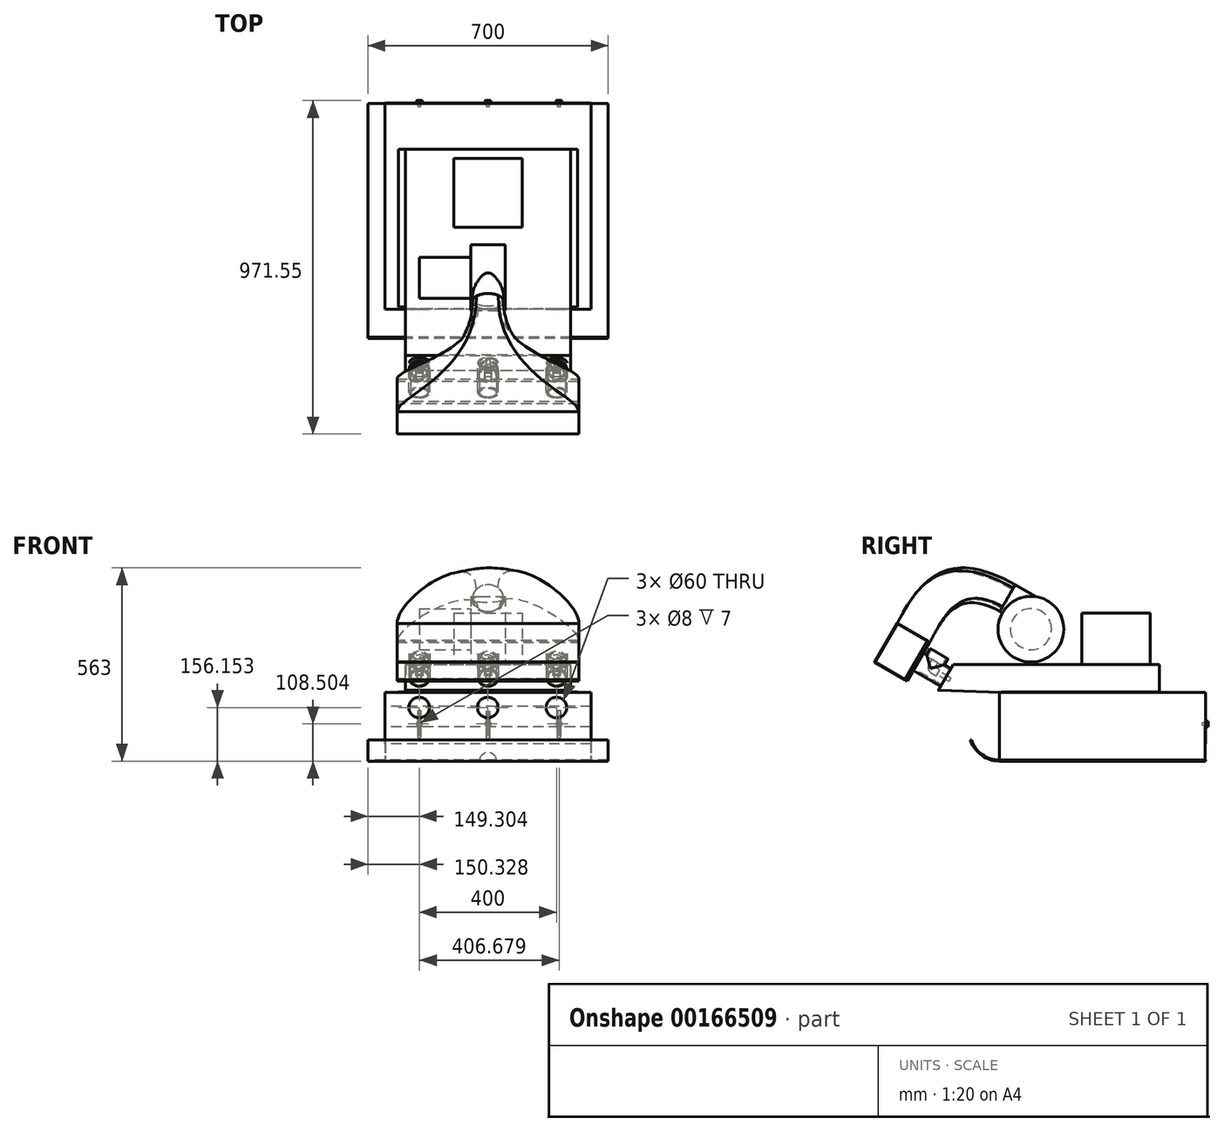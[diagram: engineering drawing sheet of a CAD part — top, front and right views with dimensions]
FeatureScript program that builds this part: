
annotation { "Feature Type Name" : "Feature", "Feature Type Description" : "" }
export const myFeature = defineFeature(function(context is Context, id is Id, definition is map)
    precondition{}
    {
        {
            assignVariable(context, id + "F0", {"name" : "Width", "anyValue" : 600});
        }
        {
            assignVariable(context, id + "F1", {"name" : "Height", "anyValue" : 200});
        }
        {
            var Q0;
            Q0=qCreatedBy(makeId("Top.planeOp"),FACE);
            var sketch = newSketch(context, id + "F2", { "sketchPlane" : qUnion([Q0])});
            skLineSegment(sketch, "E0.bottom", {"start": v(300, -300) * mm, "end": v(-300, -300) * mm});
            skLineSegment(sketch, "E0.top", {"start": v(300, 300) * mm, "end": v(-300, 300) * mm});
            skLineSegment(sketch, "E0.left", {"start": v(300, -300) * mm, "end": v(300, 300) * mm});
            skLineSegment(sketch, "E0.right", {"start": v(-300, -300) * mm, "end": v(-300, 300) * mm});
            skPoint(sketch, "E0.middle", {"position": v(0, 0) * mm});
            skSolve(sketch);
        }
        {
            var Q0;
            Q0 = qSketchRegion(id + "F2", true);
            extrude(context, id + "F3", {"entities" : qUnion([Q0]), "depth" : (getVariable(context, 'Height')) * mm});
        }
        {
            var Q0;
            Q0=makeQuery(id+"F3.opExtrude","CAP_FACE",FACE,{"disambiguationData":[OSD([sQuery(id+"F2.wireOp",EDGE,"E0.bottom"),sQuery(id+"F2.wireOp",EDGE,"E0.top"),sQuery(id+"F2.wireOp",EDGE,"E0.left"),sQuery(id+"F2.wireOp",EDGE,"E0.right")])],"isStart":true});
            shell(context, id + "F4", {"entities" : qUnion([Q0]), "thickness" : 1 * mm});
        }
        {
            var Q0;
            Q0=qCreatedBy(makeId("Front.planeOp"),FACE);
            var sketch = newSketch(context, id + "F5", { "sketchPlane" : qUnion([Q0])});
            skCircle(sketch, "E1", {"center": v(0, 0) * mm, "radius": 25 * mm});
            skCircle(sketch, "E2", {"center": v(0, 0) * mm, "radius": 23.4 * mm});
            skSolve(sketch);
        }
        {
            var Q0;
            Q0 = qSketchRegion(id + "F5", true);
            extrude(context, id + "F6", {"entities" : qUnion([Q0]), "depth" : 200 * mm});
        }
        {
            var Q0;
            Q0=makeQuery(id+"F6.opExtrude","CAP_FACE",FACE,{"disambiguationData":[OSD([sQuery(id+"F5.wireOp",EDGE,"E1"),sQuery(id+"F5.wireOp",EDGE,"E2")])],"isStart":false});
            var sketch = newSketch(context, id + "F7", { "sketchPlane" : qUnion([Q0])});
            skCircle(sketch, "E3", {"center": v(0, 0) * mm, "radius": 30 * mm});
            skSolve(sketch);
        }
        {
            var Q0;
            Q0 = qSketchRegion(id + "F7", true);
            extrude(context, id + "F8", {"entities" : qUnion([Q0]), "depth" : 100 * mm});
        }
        {
            var Q0;
            Q0=qCreatedBy(makeId("Top.planeOp"),FACE);
            var sketch = newSketch(context, id + "F9", { "sketchPlane" : qUnion([Q0])});
            skCircle(sketch, "E4", {"center": v(0, -251.88) * mm, "radius": 30 * mm});
            skSolve(sketch);
        }
        {
            var Q0;
            Q0 = qSketchRegion(id + "F9", true);
            extrude(context, id + "F10", {"entities" : qUnion([Q0]), "operationType" : NewBodyOperationType.ADD, "depth" : 50 * mm});
        }
        {
            var Q0;
            Q0=makeQuery(id+"F10.opExtrude","CAP_FACE",FACE,{"disambiguationData":[OSD([sQuery(id+"F9.wireOp",EDGE,"E4")])],"isStart":false});
            var sketch = newSketch(context, id + "F11", { "sketchPlane" : qUnion([Q0])});
            skCircle(sketch, "E5", {"center": v(0, -251.88) * mm, "radius": 25 * mm});
            skSolve(sketch);
        }
        {
            var Q0;
            Q0=makeQuery(id+"F8.opExtrude","CAP_FACE",FACE,{"disambiguationData":[OSD([sQuery(id+"F7.wireOp",EDGE,"E3")])],"isStart":false});
            var sketch = newSketch(context, id + "F12", { "sketchPlane" : qUnion([Q0])});
            skCircle(sketch, "E6", {"center": v(0, 0) * mm, "radius": 25 * mm});
            skSolve(sketch);
        }
        {
            var Q0;
            Q0 = qSketchRegion(id + "F12", true);
            extrude(context, id + "F13", {"entities" : qUnion([Q0]), "operationType" : NewBodyOperationType.REMOVE, "endBound" : BoundingType.THROUGH_ALL, "oppositeDirection" : true, "depth" : 25 * mm});
        }
        {
            var Q0;
            Q0 = qSketchRegion(id + "F11", true);
            extrude(context, id + "F14", {"entities" : qUnion([Q0]), "operationType" : NewBodyOperationType.REMOVE, "endBound" : BoundingType.UP_TO_NEXT, "oppositeDirection" : true, "depth" : 25 * mm});
        }
        {
            var Q0;
            Q0=makeQuery(id+"F10.opExtrude","CAP_FACE",FACE,{"disambiguationData":[OSD([sQuery(id+"F9.wireOp",EDGE,"E4")])],"isStart":false});
            var sketch = newSketch(context, id + "F15", { "sketchPlane" : qUnion([Q0])});
            skCircle(sketch, "E7", {"center": v(0, -251.88) * mm, "radius": 25 * mm});
            skSolve(sketch);
        }
        {
            var Q0;
            Q0 = qSketchRegion(id + "F15", true);
            extrude(context, id + "F16", {"entities" : qUnion([Q0]), "oppositeDirection" : true, "depth" : 25 * mm});
        }
        {
            var Q0;
            Q0=qCreatedBy(makeId("Right.planeOp"),FACE);
            var sketch = newSketch(context, id + "F17", { "sketchPlane" : qUnion([Q0])});
            skLineSegment(sketch, "E8", {"start": v(-261.88, 25) * mm, "end": v(-261.88, 7.92) * mm});
            skLineSegment(sketch, "E9", {"start": v(-243.95, -10) * mm, "end": v(-226.88, -10) * mm});
            skLineSegment(sketch, "E10", {"start": v(-226.88, -10) * mm, "end": v(-226.88, 10) * mm});
            skLineSegment(sketch, "E11", {"start": v(-241.88, 12.68) * mm, "end": v(-241.88, 25) * mm});
            skLineSegment(sketch, "E12", {"start": v(-241.88, 25) * mm, "end": v(-261.88, 25) * mm});
            skLineSegment(sketch, "E13.0", {"start": v(-276.88, 25) * mm, "end": v(-226.88, 25) * mm});
            skLineSegment(sketch, "E14", {"start": v(-251.88, 25) * mm, "end": v(-251.88, -30.53) * mm, "construction": true});
            skLineSegment(sketch, "E15.0", {"start": v(-200, -25) * mm, "end": v(-200, 25) * mm});
            skLineSegment(sketch, "E16", {"start": v(-200, 0) * mm, "end": v(-302.48, 0) * mm, "construction": true});
            skPoint(sketch, "E16.endSnap0", {"position": v(-200, 0) * mm});
            skArc(sketch, "E17", {"start": v(-243.95, -10) * mm, "mid": v(-256.63, -4.75) * mm, "end": v(-261.88, 7.92) * mm});
            skLineSegment(sketch, "E18", {"start": v(-226.88, 10) * mm, "end": v(-239.2, 10) * mm});
            skArc(sketch, "E19", {"start": v(-239.2, 10) * mm, "mid": v(-241.1, 10.79) * mm, "end": v(-241.88, 12.68) * mm});
            skSolve(sketch);
        }
        {
            var Q0;
            Q0 = qSketchRegion(id + "F17", true);
            extrude(context, id + "F18", {"entities" : qUnion([Q0]), "endBound" : BoundingType.SYMMETRIC, "depth" : 20 * mm});
        }
        {
            var Q0;
            Q0=makeQuery(id+"F18.opExtrude","SWEPT_FACE",FACE,{"disambiguationData":[OSD([sQuery(id+"F17.wireOp",EDGE,"E10")])]});
            var sketch = newSketch(context, id + "F19", { "sketchPlane" : qUnion([Q0])});
            skCircle(sketch, "E20", {"center": v(0, 0) * mm, "radius": 6 * mm});
            skSolve(sketch);
        }
        {
            var Q0;
            Q0 = qSketchRegion(id + "F19", true);
            extrude(context, id + "F20", {"entities" : qUnion([Q0]), "depth" : 40 * mm});
        }
        {
            var Q0;
            Q0=makeQuery(id+"F6.opExtrude","SWEPT_BODY",BODY,{"disambiguationData":[OSD([sQuery(id+"F5.wireOp",EDGE,"E1"),sQuery(id+"F5.wireOp",EDGE,"E2")])]});
            var Q1;
            Q1=makeQuery(id+"F8.opExtrude","SWEPT_BODY",BODY,{"disambiguationData":[OSD([sQuery(id+"F7.wireOp",EDGE,"E3")])]});
            var Q2;
            Q2=makeQuery(id+"F16.opExtrude","SWEPT_BODY",BODY,{"disambiguationData":[OSD([sQuery(id+"F15.wireOp",EDGE,"E7")])]});
            var Q3;
            Q3=makeQuery(id+"F18.opExtrude","SWEPT_BODY",BODY,{"disambiguationData":[OSD([sQuery(id+"F17.wireOp",EDGE,"E8"),sQuery(id+"F17.wireOp",EDGE,"E9"),sQuery(id+"F17.wireOp",EDGE,"E10"),sQuery(id+"F17.wireOp",EDGE,"E11"),sQuery(id+"F17.wireOp",EDGE,"E13.0"),sQuery(id+"F17.wireOp",EDGE,"E17"),sQuery(id+"F17.wireOp",EDGE,"E18"),sQuery(id+"F17.wireOp",EDGE,"E19")])]});
            var Q4;
            Q4=makeQuery(id+"F20.opExtrude","SWEPT_BODY",BODY,{"disambiguationData":[OSD([sQuery(id+"F19.wireOp",EDGE,"E20")])]});
            transform(context, id + "F21", {"entities" : qUnion([Q0, Q1, Q2, Q3, Q4]), "transformType" : TransformType.TRANSLATION_3D, "dx" : 0 * mm, "dy" : -282 * mm, "dz" : 163 * mm, "makeCopy" : false});
        }
        {
            var Q0;
            Q0=makeQuery(id+"F6.opExtrude","SWEPT_BODY",BODY,{"disambiguationData":[OSD([sQuery(id+"F5.wireOp",EDGE,"E1"),sQuery(id+"F5.wireOp",EDGE,"E2")])]});
            var Q1;
            Q1=makeQuery(id+"F8.opExtrude","SWEPT_BODY",BODY,{"disambiguationData":[OSD([sQuery(id+"F7.wireOp",EDGE,"E3")])]});
            var Q2;
            Q2=makeQuery(id+"F16.opExtrude","SWEPT_BODY",BODY,{"disambiguationData":[OSD([sQuery(id+"F15.wireOp",EDGE,"E7")])]});
            var Q3;
            Q3=makeQuery(id+"F18.opExtrude","SWEPT_BODY",BODY,{"disambiguationData":[OSD([sQuery(id+"F17.wireOp",EDGE,"E8"),sQuery(id+"F17.wireOp",EDGE,"E9"),sQuery(id+"F17.wireOp",EDGE,"E10"),sQuery(id+"F17.wireOp",EDGE,"E11"),sQuery(id+"F17.wireOp",EDGE,"E13.0"),sQuery(id+"F17.wireOp",EDGE,"E17"),sQuery(id+"F17.wireOp",EDGE,"E18"),sQuery(id+"F17.wireOp",EDGE,"E19")])]});
            var Q4;
            Q4=makeQuery(id+"F20.opExtrude","SWEPT_BODY",BODY,{"disambiguationData":[OSD([sQuery(id+"F19.wireOp",EDGE,"E20")])]});
            transform(context, id + "F22", {"entities" : qUnion([Q0, Q1, Q2, Q3, Q4]), "transformType" : TransformType.TRANSLATION_3D, "dx" : 200 * mm, "dy" : 0 * mm, "dz" : 0 * mm, "makeCopy" : true});
        }
        {
            var Q0;
            Q0=makeQuery(id+"F6.opExtrude","SWEPT_BODY",BODY,{"disambiguationData":[OSD([sQuery(id+"F5.wireOp",EDGE,"E1"),sQuery(id+"F5.wireOp",EDGE,"E2")])]});
            var Q1;
            Q1=makeQuery(id+"F8.opExtrude","SWEPT_BODY",BODY,{"disambiguationData":[OSD([sQuery(id+"F7.wireOp",EDGE,"E3")])]});
            var Q2;
            Q2=makeQuery(id+"F16.opExtrude","SWEPT_BODY",BODY,{"disambiguationData":[OSD([sQuery(id+"F15.wireOp",EDGE,"E7")])]});
            var Q3;
            Q3=makeQuery(id+"F18.opExtrude","SWEPT_BODY",BODY,{"disambiguationData":[OSD([sQuery(id+"F17.wireOp",EDGE,"E8"),sQuery(id+"F17.wireOp",EDGE,"E9"),sQuery(id+"F17.wireOp",EDGE,"E10"),sQuery(id+"F17.wireOp",EDGE,"E11"),sQuery(id+"F17.wireOp",EDGE,"E13.0"),sQuery(id+"F17.wireOp",EDGE,"E17"),sQuery(id+"F17.wireOp",EDGE,"E18"),sQuery(id+"F17.wireOp",EDGE,"E19")])]});
            var Q4;
            Q4=makeQuery(id+"F20.opExtrude","SWEPT_BODY",BODY,{"disambiguationData":[OSD([sQuery(id+"F19.wireOp",EDGE,"E20")])]});
            transform(context, id + "F23", {"entities" : qUnion([Q0, Q1, Q2, Q3, Q4]), "transformType" : TransformType.TRANSLATION_3D, "dx" : -200 * mm, "dy" : 0 * mm, "dz" : 0 * mm, "makeCopy" : true});
        }
        {
            var Q0;
            Q0=makeQuery(id+"F6.opExtrude","SWEPT_BODY",BODY,{"disambiguationData":[OSD([sQuery(id+"F5.wireOp",EDGE,"E1"),sQuery(id+"F5.wireOp",EDGE,"E2")])]});
            var Q1;
            Q1=makeQuery(id+"F8.opExtrude","SWEPT_BODY",BODY,{"disambiguationData":[OSD([sQuery(id+"F7.wireOp",EDGE,"E3")])]});
            var Q2;
            Q2=makeQuery(id+"F22.opPattern","COPY",BODY,{"derivedFrom":makeQuery(id+"F8.opExtrude","SWEPT_BODY",BODY,{"disambiguationData":[OSD([sQuery(id+"F7.wireOp",EDGE,"E3")])]}),"instanceName":"1"});
            var Q3;
            Q3=makeQuery(id+"F22.opPattern","COPY",BODY,{"derivedFrom":makeQuery(id+"F6.opExtrude","SWEPT_BODY",BODY,{"disambiguationData":[OSD([sQuery(id+"F5.wireOp",EDGE,"E1"),sQuery(id+"F5.wireOp",EDGE,"E2")])]}),"instanceName":"1"});
            var Q4;
            Q4=makeQuery(id+"F23.opPattern","COPY",BODY,{"derivedFrom":makeQuery(id+"F8.opExtrude","SWEPT_BODY",BODY,{"disambiguationData":[OSD([sQuery(id+"F7.wireOp",EDGE,"E3")])]}),"instanceName":"1"});
            var Q5;
            Q5=makeQuery(id+"F23.opPattern","COPY",BODY,{"derivedFrom":makeQuery(id+"F6.opExtrude","SWEPT_BODY",BODY,{"disambiguationData":[OSD([sQuery(id+"F5.wireOp",EDGE,"E1"),sQuery(id+"F5.wireOp",EDGE,"E2")])]}),"instanceName":"1"});
            var Q6;
            Q6=makeQuery(id+"F16.opExtrude","SWEPT_BODY",BODY,{"disambiguationData":[OSD([sQuery(id+"F15.wireOp",EDGE,"E7")])]});
            var Q7;
            Q7=makeQuery(id+"F18.opExtrude","SWEPT_BODY",BODY,{"disambiguationData":[OSD([sQuery(id+"F17.wireOp",EDGE,"E8"),sQuery(id+"F17.wireOp",EDGE,"E9"),sQuery(id+"F17.wireOp",EDGE,"E10"),sQuery(id+"F17.wireOp",EDGE,"E11"),sQuery(id+"F17.wireOp",EDGE,"E13.0"),sQuery(id+"F17.wireOp",EDGE,"E17"),sQuery(id+"F17.wireOp",EDGE,"E18"),sQuery(id+"F17.wireOp",EDGE,"E19")])]});
            var Q8;
            Q8=makeQuery(id+"F20.opExtrude","SWEPT_BODY",BODY,{"disambiguationData":[OSD([sQuery(id+"F19.wireOp",EDGE,"E20")])]});
            var Q9;
            Q9=makeQuery(id+"F22.opPattern","COPY",BODY,{"derivedFrom":makeQuery(id+"F20.opExtrude","SWEPT_BODY",BODY,{"disambiguationData":[OSD([sQuery(id+"F19.wireOp",EDGE,"E20")])]}),"instanceName":"1"});
            var Q10;
            Q10=makeQuery(id+"F22.opPattern","COPY",BODY,{"derivedFrom":makeQuery(id+"F18.opExtrude","SWEPT_BODY",BODY,{"disambiguationData":[OSD([sQuery(id+"F17.wireOp",EDGE,"E8"),sQuery(id+"F17.wireOp",EDGE,"E9"),sQuery(id+"F17.wireOp",EDGE,"E10"),sQuery(id+"F17.wireOp",EDGE,"E11"),sQuery(id+"F17.wireOp",EDGE,"E13.0"),sQuery(id+"F17.wireOp",EDGE,"E17"),sQuery(id+"F17.wireOp",EDGE,"E18"),sQuery(id+"F17.wireOp",EDGE,"E19")])]}),"instanceName":"1"});
            var Q11;
            Q11=makeQuery(id+"F22.opPattern","COPY",BODY,{"derivedFrom":makeQuery(id+"F16.opExtrude","SWEPT_BODY",BODY,{"disambiguationData":[OSD([sQuery(id+"F15.wireOp",EDGE,"E7")])]}),"instanceName":"1"});
            var Q12;
            Q12=makeQuery(id+"F23.opPattern","COPY",BODY,{"derivedFrom":makeQuery(id+"F20.opExtrude","SWEPT_BODY",BODY,{"disambiguationData":[OSD([sQuery(id+"F19.wireOp",EDGE,"E20")])]}),"instanceName":"1"});
            var Q13;
            Q13=makeQuery(id+"F23.opPattern","COPY",BODY,{"derivedFrom":makeQuery(id+"F18.opExtrude","SWEPT_BODY",BODY,{"disambiguationData":[OSD([sQuery(id+"F17.wireOp",EDGE,"E8"),sQuery(id+"F17.wireOp",EDGE,"E9"),sQuery(id+"F17.wireOp",EDGE,"E10"),sQuery(id+"F17.wireOp",EDGE,"E11"),sQuery(id+"F17.wireOp",EDGE,"E13.0"),sQuery(id+"F17.wireOp",EDGE,"E17"),sQuery(id+"F17.wireOp",EDGE,"E18"),sQuery(id+"F17.wireOp",EDGE,"E19")])]}),"instanceName":"1"});
            var Q14;
            Q14=makeQuery(id+"F23.opPattern","COPY",BODY,{"derivedFrom":makeQuery(id+"F16.opExtrude","SWEPT_BODY",BODY,{"disambiguationData":[OSD([sQuery(id+"F15.wireOp",EDGE,"E7")])]}),"instanceName":"1"});
            var Q15;
            Q15=makeQuery(id+"F3.opExtrude","CAP_EDGE",EDGE,{"disambiguationData":[OSD([sQuery(id+"F2.wireOp",EDGE,"E0.bottom")])],"isStart":false});
            transform(context, id + "F24", {"entities" : qUnion([Q0, Q1, Q2, Q3, Q4, Q5, Q6, Q7, Q8, Q9, Q10, Q11, Q12, Q13, Q14]), "transformType" : TransformType.ROTATION, "transformAxis" : qUnion([Q15]), "angle" : 30 * degree, "makeCopy" : false});
        }
        {
            var Q0;
            Q0=makeQuery(id+"F3.opExtrude","SWEPT_FACE",FACE,{"disambiguationData":[OSD([sQuery(id+"F2.wireOp",EDGE,"E0.bottom")])]});
            var sketch = newSketch(context, id + "F25", { "sketchPlane" : qUnion([Q0])});
            skCircle(sketch, "E21", {"center": v(-200.7, 156.15) * mm, "radius": 30 * mm});
            skCircle(sketch, "E22.1.0.0", {"center": v(-0.7, 156.15) * mm, "radius": 30 * mm});
            skCircle(sketch, "E22.2.0.0", {"center": v(199.3, 156.15) * mm, "radius": 30 * mm});
            skLineSegment(sketch, "E22.direction1", {"start": v(-200.7, 156.15) * mm, "end": v(-0.7, 156.15) * mm, "construction": true});
            skSolve(sketch);
        }
        {
            var Q0;
            Q0 = qSketchRegion(id + "F25", true);
            extrude(context, id + "F26", {"entities" : qUnion([Q0]), "operationType" : NewBodyOperationType.REMOVE, "oppositeDirection" : true, "depth" : 25 * mm});
        }
        {
            var Q0;
            Q0=makeQuery(id+"F6.opExtrude","SWEPT_BODY",BODY,{"disambiguationData":[OSD([sQuery(id+"F5.wireOp",EDGE,"E1"),sQuery(id+"F5.wireOp",EDGE,"E2")])]});
            var Q1;
            Q1=makeQuery(id+"F8.opExtrude","SWEPT_BODY",BODY,{"disambiguationData":[OSD([sQuery(id+"F7.wireOp",EDGE,"E3")])]});
            var Q2;
            Q2=makeQuery(id+"F22.opPattern","COPY",BODY,{"derivedFrom":makeQuery(id+"F18.opExtrude","SWEPT_BODY",BODY,{"disambiguationData":[OSD([sQuery(id+"F17.wireOp",EDGE,"E8"),sQuery(id+"F17.wireOp",EDGE,"E9"),sQuery(id+"F17.wireOp",EDGE,"E10"),sQuery(id+"F17.wireOp",EDGE,"E11"),sQuery(id+"F17.wireOp",EDGE,"E13.0"),sQuery(id+"F17.wireOp",EDGE,"E17"),sQuery(id+"F17.wireOp",EDGE,"E18"),sQuery(id+"F17.wireOp",EDGE,"E19")])]}),"instanceName":"1"});
            var Q3;
            Q3=makeQuery(id+"F22.opPattern","COPY",BODY,{"derivedFrom":makeQuery(id+"F16.opExtrude","SWEPT_BODY",BODY,{"disambiguationData":[OSD([sQuery(id+"F15.wireOp",EDGE,"E7")])]}),"instanceName":"1"});
            var Q4;
            Q4=makeQuery(id+"F22.opPattern","COPY",BODY,{"derivedFrom":makeQuery(id+"F8.opExtrude","SWEPT_BODY",BODY,{"disambiguationData":[OSD([sQuery(id+"F7.wireOp",EDGE,"E3")])]}),"instanceName":"1"});
            var Q5;
            Q5=makeQuery(id+"F22.opPattern","COPY",BODY,{"derivedFrom":makeQuery(id+"F6.opExtrude","SWEPT_BODY",BODY,{"disambiguationData":[OSD([sQuery(id+"F5.wireOp",EDGE,"E1"),sQuery(id+"F5.wireOp",EDGE,"E2")])]}),"instanceName":"1"});
            var Q6;
            Q6=makeQuery(id+"F23.opPattern","COPY",BODY,{"derivedFrom":makeQuery(id+"F8.opExtrude","SWEPT_BODY",BODY,{"disambiguationData":[OSD([sQuery(id+"F7.wireOp",EDGE,"E3")])]}),"instanceName":"1"});
            var Q7;
            Q7=makeQuery(id+"F23.opPattern","COPY",BODY,{"derivedFrom":makeQuery(id+"F6.opExtrude","SWEPT_BODY",BODY,{"disambiguationData":[OSD([sQuery(id+"F5.wireOp",EDGE,"E1"),sQuery(id+"F5.wireOp",EDGE,"E2")])]}),"instanceName":"1"});
            var Q8;
            Q8=makeQuery(id+"F16.opExtrude","SWEPT_BODY",BODY,{"disambiguationData":[OSD([sQuery(id+"F15.wireOp",EDGE,"E7")])]});
            var Q9;
            Q9=makeQuery(id+"F18.opExtrude","SWEPT_BODY",BODY,{"disambiguationData":[OSD([sQuery(id+"F17.wireOp",EDGE,"E8"),sQuery(id+"F17.wireOp",EDGE,"E9"),sQuery(id+"F17.wireOp",EDGE,"E10"),sQuery(id+"F17.wireOp",EDGE,"E11"),sQuery(id+"F17.wireOp",EDGE,"E13.0"),sQuery(id+"F17.wireOp",EDGE,"E17"),sQuery(id+"F17.wireOp",EDGE,"E18"),sQuery(id+"F17.wireOp",EDGE,"E19")])]});
            var Q10;
            Q10=makeQuery(id+"F20.opExtrude","SWEPT_BODY",BODY,{"disambiguationData":[OSD([sQuery(id+"F19.wireOp",EDGE,"E20")])]});
            var Q11;
            Q11=makeQuery(id+"F22.opPattern","COPY",BODY,{"derivedFrom":makeQuery(id+"F20.opExtrude","SWEPT_BODY",BODY,{"disambiguationData":[OSD([sQuery(id+"F19.wireOp",EDGE,"E20")])]}),"instanceName":"1"});
            var Q12;
            Q12=makeQuery(id+"F23.opPattern","COPY",BODY,{"derivedFrom":makeQuery(id+"F20.opExtrude","SWEPT_BODY",BODY,{"disambiguationData":[OSD([sQuery(id+"F19.wireOp",EDGE,"E20")])]}),"instanceName":"1"});
            var Q13;
            Q13=makeQuery(id+"F23.opPattern","COPY",BODY,{"derivedFrom":makeQuery(id+"F18.opExtrude","SWEPT_BODY",BODY,{"disambiguationData":[OSD([sQuery(id+"F17.wireOp",EDGE,"E8"),sQuery(id+"F17.wireOp",EDGE,"E9"),sQuery(id+"F17.wireOp",EDGE,"E10"),sQuery(id+"F17.wireOp",EDGE,"E11"),sQuery(id+"F17.wireOp",EDGE,"E13.0"),sQuery(id+"F17.wireOp",EDGE,"E17"),sQuery(id+"F17.wireOp",EDGE,"E18"),sQuery(id+"F17.wireOp",EDGE,"E19")])]}),"instanceName":"1"});
            var Q14;
            Q14=makeQuery(id+"F23.opPattern","COPY",BODY,{"derivedFrom":makeQuery(id+"F16.opExtrude","SWEPT_BODY",BODY,{"disambiguationData":[OSD([sQuery(id+"F15.wireOp",EDGE,"E7")])]}),"instanceName":"1"});
            transform(context, id + "F27", {"entities" : qUnion([Q0, Q1, Q2, Q3, Q4, Q5, Q6, Q7, Q8, Q9, Q10, Q11, Q12, Q13, Q14]), "transformType" : TransformType.TRANSLATION_3D, "dx" : 0 * mm, "dy" : 20 * mm, "dz" : -15 * mm, "makeCopy" : false});
        }
        {
            var Q0;
            Q0=makeQuery(id+"F3.opExtrude","SWEPT_FACE",FACE,{"disambiguationData":[OSD([sQuery(id+"F2.wireOp",EDGE,"E0.top")])]});
            var sketch = newSketch(context, id + "F28", { "sketchPlane" : qUnion([Q0])});
            skLineSegment(sketch, "E23.bottom", {"start": v(-300, 0) * mm, "end": v(300, 0) * mm});
            skLineSegment(sketch, "E23.top", {"start": v(-300, 100) * mm, "end": v(300, 100) * mm});
            skLineSegment(sketch, "E23.left", {"start": v(-300, 0) * mm, "end": v(-300, 100) * mm});
            skLineSegment(sketch, "E23.right", {"start": v(300, 0) * mm, "end": v(300, 100) * mm});
            skSolve(sketch);
        }
        {
            var Q0;
            Q0 = qSketchRegion(id + "F28", true);
            var Q1;
            Q1=makeQuery(id+"F4.opShell","OFFSET_FACE",FACE,{"disambiguationData":[OSD([sQuery(id+"F2.wireOp",EDGE,"E0.top")])]});
            var Q2;
            Q2=makeQuery(id+"F3.opExtrude","SWEPT_BODY",BODY,{"disambiguationData":[OSD([sQuery(id+"F2.wireOp",EDGE,"E0.bottom"),sQuery(id+"F2.wireOp",EDGE,"E0.top"),sQuery(id+"F2.wireOp",EDGE,"E0.left"),sQuery(id+"F2.wireOp",EDGE,"E0.right")])]});
            extrude(context, id + "F29", {"entities" : qUnion([Q0]), "operationType" : NewBodyOperationType.REMOVE, "endBound" : BoundingType.UP_TO_SURFACE, "oppositeDirection" : true, "endBoundEntityFace" : qUnion([Q1]), "endBoundEntityBody" : qUnion([Q2]), "depth" : 25 * mm});
        }
        {
            var Q0;
            Q0=makeQuery(id+"F3.opExtrude","SWEPT_FACE",FACE,{"disambiguationData":[OSD([sQuery(id+"F2.wireOp",EDGE,"E0.top")])]});
            var sketch = newSketch(context, id + "F30", { "sketchPlane" : qUnion([Q0])});
            skPoint(sketch, "E24.firstSnap0", {"position": v(-300, 150) * mm});
            skLineSegment(sketch, "E24.bottom", {"start": v(-300, 50.17) * mm, "end": v(300, 50.17) * mm});
            skLineSegment(sketch, "E24.top", {"start": v(-300, 160.17) * mm, "end": v(300, 160.17) * mm});
            skLineSegment(sketch, "E24.left", {"start": v(-300, 50.17) * mm, "end": v(-300, 160.17) * mm});
            skLineSegment(sketch, "E24.right", {"start": v(300, 50.17) * mm, "end": v(300, 160.17) * mm});
            skSolve(sketch);
        }
        {
            var Q0;
            Q0 = qSketchRegion(id + "F30", true);
            extrude(context, id + "F31", {"entities" : qUnion([Q0]), "depth" : 1 * mm});
        }
        {
            var Q0;
            Q0=qCreatedBy(makeId("Top.planeOp"),FACE);
            var sketch = newSketch(context, id + "F32", { "sketchPlane" : qUnion([Q0])});
            skLineSegment(sketch, "E25.bottom", {"start": v(350, -300) * mm, "end": v(300, -300) * mm});
            skLineSegment(sketch, "E25.top", {"start": v(350, 300) * mm, "end": v(300, 300) * mm});
            skLineSegment(sketch, "E25.left", {"start": v(350, -300) * mm, "end": v(350, 300) * mm});
            skLineSegment(sketch, "E25.right", {"start": v(300, -300) * mm, "end": v(300, 300) * mm});
            skLineSegment(sketch, "E26.bottom", {"start": v(-300, -300) * mm, "end": v(-350, -300) * mm});
            skLineSegment(sketch, "E26.top", {"start": v(-300, 300) * mm, "end": v(-350, 300) * mm});
            skLineSegment(sketch, "E26.left", {"start": v(-300, -300) * mm, "end": v(-300, 300) * mm});
            skLineSegment(sketch, "E26.right", {"start": v(-350, -300) * mm, "end": v(-350, 300) * mm});
            skSolve(sketch);
        }
        {
            var Q0;
            Q0 = qSketchRegion(id + "F32", true);
            extrude(context, id + "F33", {"entities" : qUnion([Q0]), "operationType" : NewBodyOperationType.ADD, "depth" : 3 * mm});
        }
        {
            var Q0;
            Q0=qCreatedBy(makeId("Right.planeOp"),FACE);
            var sketch = newSketch(context, id + "F34", { "sketchPlane" : qUnion([Q0])});
            skArc(sketch, "E27", {"start": v(-300, 0) * mm, "mid": v(-352.3, 16.96) * mm, "end": v(-384.68, 61.4) * mm});
            skArc(sketch, "E28", {"start": v(-300, 3) * mm, "mid": v(-350.45, 19.33) * mm, "end": v(-381.76, 62.14) * mm});
            skLineSegment(sketch, "E29", {"start": v(-384.68, 61.4) * mm, "end": v(-381.76, 62.14) * mm});
            skLineSegment(sketch, "E30", {"start": v(-300, 3) * mm, "end": v(-300, 0) * mm});
            skSolve(sketch);
        }
        {
            var Q0;
            Q0 = qSketchRegion(id + "F34", true);
            extrude(context, id + "F35", {"entities" : qUnion([Q0]), "operationType" : NewBodyOperationType.ADD, "endBound" : BoundingType.SYMMETRIC, "depth" : (getVariable(context, 'Width') + 2 * 50) * mm});
        }
        {
            var Q0;
            Q0=makeQuery(id+"F31.opExtrude","CAP_FACE",FACE,{"disambiguationData":[OSD([sQuery(id+"F30.wireOp",EDGE,"E24.bottom"),sQuery(id+"F30.wireOp",EDGE,"E24.top"),sQuery(id+"F30.wireOp",EDGE,"E24.left"),sQuery(id+"F30.wireOp",EDGE,"E24.right")])],"isStart":false});
            var sketch = newSketch(context, id + "F36", { "sketchPlane" : qUnion([Q0])});
            skLineSegment(sketch, "E31.bottom", {"start": v(4, 65.13) * mm, "end": v(-4, 65.13) * mm});
            skLineSegment(sketch, "E31.top", {"start": v(4, 145.13) * mm, "end": v(-4, 145.13) * mm});
            skLineSegment(sketch, "E31.left", {"start": v(4, 65.13) * mm, "end": v(4, 145.13) * mm});
            skLineSegment(sketch, "E31.right", {"start": v(-4, 65.13) * mm, "end": v(-4, 145.13) * mm});
            skPoint(sketch, "E31.middle", {"position": v(0, 105.13) * mm});
            skPoint(sketch, "E31.middle.positionSnap0", {"position": v(0, 50.17) * mm});
            skPoint(sketch, "E31.centerSnap0", {"position": v(0, 50.17) * mm});
            skLineSegment(sketch, "E32.bottom", {"start": v(203.67, 68.5) * mm, "end": v(195.67, 68.5) * mm});
            skLineSegment(sketch, "E32.top", {"start": v(203.67, 148.5) * mm, "end": v(195.67, 148.5) * mm});
            skLineSegment(sketch, "E32.left", {"start": v(203.67, 68.5) * mm, "end": v(203.67, 148.5) * mm});
            skLineSegment(sketch, "E32.right", {"start": v(195.67, 68.5) * mm, "end": v(195.67, 148.5) * mm});
            skPoint(sketch, "E32.middle", {"position": v(199.67, 108.5) * mm});
            skLineSegment(sketch, "E33.bottom", {"start": v(-203, 68.5) * mm, "end": v(-211, 68.5) * mm});
            skLineSegment(sketch, "E33.top", {"start": v(-203, 148.5) * mm, "end": v(-211, 148.5) * mm});
            skLineSegment(sketch, "E33.left", {"start": v(-203, 68.5) * mm, "end": v(-203, 148.5) * mm});
            skLineSegment(sketch, "E33.right", {"start": v(-211, 68.5) * mm, "end": v(-211, 148.5) * mm});
            skPoint(sketch, "E33.middle", {"position": v(-207, 108.5) * mm});
            skPoint(sketch, "E33.cornerSnap0", {"position": v(199.67, 68.5) * mm});
            skSolve(sketch);
        }
        {
            var Q0;
            Q0 = qSketchRegion(id + "F36", true);
            extrude(context, id + "F37", {"entities" : qUnion([Q0]), "operationType" : NewBodyOperationType.REMOVE, "endBound" : BoundingType.UP_TO_NEXT, "oppositeDirection" : true, "depth" : 25 * mm});
        }
        {
            var Q0;
            Q0 = qSketchRegion(id + "F36", true);
            var Q1;
            Q1=makeQuery(id+"F3.opExtrude","SWEPT_FACE",FACE,{"disambiguationData":[OSD([sQuery(id+"F2.wireOp",EDGE,"E0.top")])]});
            var Q2;
            Q2=makeQuery(id+"F3.opExtrude","SWEPT_BODY",BODY,{"disambiguationData":[OSD([sQuery(id+"F2.wireOp",EDGE,"E0.bottom"),sQuery(id+"F2.wireOp",EDGE,"E0.top"),sQuery(id+"F2.wireOp",EDGE,"E0.left"),sQuery(id+"F2.wireOp",EDGE,"E0.right")])]});
            extrude(context, id + "F38", {"entities" : qUnion([Q0]), "operationType" : NewBodyOperationType.REMOVE, "endBound" : BoundingType.UP_TO_SURFACE, "oppositeDirection" : true, "endBoundEntityFace" : qUnion([Q1]), "endBoundEntityBody" : qUnion([Q2]), "depth" : 25 * mm});
        }
        {
            var Q0;
            Q0=makeQuery(id+"F31.opExtrude","CAP_FACE",FACE,{"disambiguationData":[OSD([sQuery(id+"F30.wireOp",EDGE,"E24.bottom"),sQuery(id+"F30.wireOp",EDGE,"E24.top"),sQuery(id+"F30.wireOp",EDGE,"E24.left"),sQuery(id+"F30.wireOp",EDGE,"E24.right")])],"isStart":false});
            var sketch = newSketch(context, id + "F39", { "sketchPlane" : qUnion([Q0])});
            skCircle(sketch, "E34", {"center": v(-207, 108.5) * mm, "radius": 4 * mm});
            skPoint(sketch, "E34.centerSnap0", {"position": v(-207, 148.5) * mm});
            skCircle(sketch, "E35", {"center": v(0, 108.5) * mm, "radius": 4 * mm});
            skCircle(sketch, "E36", {"center": v(199.67, 108.5) * mm, "radius": 4 * mm});
            skPoint(sketch, "E36.centerSnap0", {"position": v(199.67, 68.5) * mm});
            skPoint(sketch, "E36.centerSnap1", {"position": v(203.67, 108.5) * mm});
            skSolve(sketch);
        }
        {
            var Q0;
            Q0 = qSketchRegion(id + "F39", true);
            extrude(context, id + "F40", {"entities" : qUnion([Q0]), "oppositeDirection" : true, "depth" : 10 * mm});
        }
        {
            var Q0;
            Q0=makeQuery(id+"F31.opExtrude","CAP_FACE",FACE,{"disambiguationData":[OSD([sQuery(id+"F30.wireOp",EDGE,"E24.bottom"),sQuery(id+"F30.wireOp",EDGE,"E24.top"),sQuery(id+"F30.wireOp",EDGE,"E24.left"),sQuery(id+"F30.wireOp",EDGE,"E24.right")])],"isStart":false});
            var sketch = newSketch(context, id + "F41", { "sketchPlane" : qUnion([Q0])});
            skCircle(sketch, "E37.0.0", {"center": v(-207, 108.5) * mm, "radius": 4 * mm});
            skCircle(sketch, "E38.0.0", {"center": v(0, 108.5) * mm, "radius": 4 * mm});
            skCircle(sketch, "E39.0.0", {"center": v(199.67, 108.5) * mm, "radius": 4 * mm});
            skCircle(sketch, "E40", {"center": v(199.67, 108.5) * mm, "radius": 8.5 * mm});
            skCircle(sketch, "E41", {"center": v(0, 108.5) * mm, "radius": 8.5 * mm});
            skCircle(sketch, "E42", {"center": v(-207, 108.5) * mm, "radius": 8.5 * mm});
            skSolve(sketch);
        }
        {
            var Q0;
            Q0 = qSketchRegion(id + "F41", true);
            extrude(context, id + "F42", {"entities" : qUnion([Q0]), "operationType" : NewBodyOperationType.ADD, "depth" : 7 * mm});
        }
        {
            var Q0;
            Q0=makeQuery(id+"F8.opExtrude","CAP_FACE",FACE,{"disambiguationData":[OSD([sQuery(id+"F7.wireOp",EDGE,"E3")])],"isStart":true});
            var sketch = newSketch(context, id + "F43", { "sketchPlane" : qUnion([Q0])});
            skLineSegment(sketch, "E43.bottom", {"start": v(240, -60.57) * mm, "end": v(-240, -60.57) * mm});
            skLineSegment(sketch, "E43.top", {"start": v(240, 27) * mm, "end": v(-240, 27) * mm});
            skLineSegment(sketch, "E43.left", {"start": v(240, -60.57) * mm, "end": v(240, 27) * mm});
            skLineSegment(sketch, "E43.right", {"start": v(-240, -60.57) * mm, "end": v(-240, 27) * mm});
            skPoint(sketch, "E43.middle", {"position": v(0, -16.79) * mm});
            skCircle(sketch, "E44.0", {"center": v(-200, -16.79) * mm, "radius": 25 * mm});
            skCircle(sketch, "E45.0", {"center": v(0, -16.79) * mm, "radius": 25 * mm});
            skCircle(sketch, "E46.0", {"center": v(200, -16.79) * mm, "radius": 25 * mm});
            skSolve(sketch);
        }
        {
            var Q0;
            Q0 = qSketchRegion(id + "F43", true);
            extrude(context, id + "F44", {"entities" : qUnion([Q0]), "depth" : 1 * mm});
        }
        {
            var Q0;
            Q0=makeQuery(id+"F3.opExtrude","SWEPT_FACE",FACE,{"disambiguationData":[OSD([sQuery(id+"F2.wireOp",EDGE,"E0.right")])]});
            var sketch = newSketch(context, id + "F45", { "sketchPlane" : qUnion([Q0])});
            skPoint(sketch, "E47.0", {"position": v(434.22, 281.88) * mm});
            skLineSegment(sketch, "E48.bottom", {"start": v(434.22, 281.88) * mm, "end": v(-165.78, 281.88) * mm});
            skLineSegment(sketch, "E48.top", {"start": v(434.22, 280.88) * mm, "end": v(-165.78, 280.88) * mm});
            skLineSegment(sketch, "E48.left", {"start": v(434.22, 281.88) * mm, "end": v(434.22, 280.88) * mm});
            skLineSegment(sketch, "E48.right", {"start": v(-165.78, 281.88) * mm, "end": v(-165.78, 280.88) * mm});
            skSolve(sketch);
        }
        {
            var Q0;
            Q0 = qSketchRegion(id + "F45", true);
            extrude(context, id + "F46", {"entities" : qUnion([Q0]), "oppositeDirection" : true, "depth" : 480 * mm});
        }
        {
            var Q0;
            Q0=makeQuery(id+"F46.opExtrude","SWEPT_BODY",BODY,{"disambiguationData":[OSD([sQuery(id+"F45.wireOp",EDGE,"E48.bottom"),sQuery(id+"F45.wireOp",EDGE,"E48.top"),sQuery(id+"F45.wireOp",EDGE,"E48.left"),sQuery(id+"F45.wireOp",EDGE,"E48.right")])]});
            var Q1;
            Q1=makeQuery(id+"F44.opExtrude","CAP_EDGE",EDGE,{"disambiguationData":[OSD([sQuery(id+"F43.wireOp",EDGE,"E43.top")])],"isStart":true});
            transform(context, id + "F47", {"entities" : qUnion([Q0]), "transformType" : TransformType.TRANSLATION_DISTANCE, "transformDirection" : qUnion([Q1]), "distance" : 60 * mm, "makeCopy" : false});
        }
        {
            var Q0;
            Q0=makeQuery(id+"F46.opExtrude","SWEPT_BODY",BODY,{"disambiguationData":[OSD([sQuery(id+"F45.wireOp",EDGE,"E48.bottom"),sQuery(id+"F45.wireOp",EDGE,"E48.top"),sQuery(id+"F45.wireOp",EDGE,"E48.left"),sQuery(id+"F45.wireOp",EDGE,"E48.right")])]});
            var Q1;
            Q1=makeQuery(id+"F44.opExtrude","SWEPT_BODY",BODY,{"disambiguationData":[OSD([sQuery(id+"F43.wireOp",EDGE,"E43.bottom"),sQuery(id+"F43.wireOp",EDGE,"E43.top"),sQuery(id+"F43.wireOp",EDGE,"E43.left"),sQuery(id+"F43.wireOp",EDGE,"E43.right"),sQuery(id+"F43.wireOp",EDGE,"E44.0"),sQuery(id+"F43.wireOp",EDGE,"E45.0"),sQuery(id+"F43.wireOp",EDGE,"E46.0")])]});
            booleanBodies(context, id + "F48", {"operationType" : BooleanOperationType.UNION, "tools" : qUnion([Q0, Q1])});
        }
        {
            var Q0;
            Q0=makeQuery(id+"F46.opExtrude","SWEPT_FACE",FACE,{"disambiguationData":[OSD([sQuery(id+"F45.wireOp",EDGE,"E48.right")])]});
            var sketch = newSketch(context, id + "F49", { "sketchPlane" : qUnion([Q0])});
            skLineSegment(sketch, "E49", {"start": v(240, 280.88) * mm, "end": v(240, 200) * mm});
            skLineSegment(sketch, "E50", {"start": v(240, 200) * mm, "end": v(261, 200) * mm});
            skLineSegment(sketch, "E51", {"start": v(261, 200) * mm, "end": v(261, 201) * mm});
            skLineSegment(sketch, "E52", {"start": v(261, 201) * mm, "end": v(241, 201) * mm});
            skLineSegment(sketch, "E53", {"start": v(241, 201) * mm, "end": v(241, 281.88) * mm});
            skLineSegment(sketch, "E54", {"start": v(241, 281.88) * mm, "end": v(240, 281.88) * mm});
            skLineSegment(sketch, "E55", {"start": v(-240, 281.88) * mm, "end": v(-240, 200) * mm});
            skLineSegment(sketch, "E56", {"start": v(-240, 200) * mm, "end": v(-261, 200) * mm});
            skLineSegment(sketch, "E57", {"start": v(-261, 200) * mm, "end": v(-261, 201) * mm});
            skLineSegment(sketch, "E58", {"start": v(-261, 201) * mm, "end": v(-241, 201) * mm});
            skLineSegment(sketch, "E59", {"start": v(-241, 201) * mm, "end": v(-241, 281.88) * mm});
            skLineSegment(sketch, "E60", {"start": v(-241, 281.88) * mm, "end": v(-240, 281.88) * mm});
            skSolve(sketch);
        }
        {
            var Q0;
            Q0 = qSketchRegion(id + "F49", true);
            var Q1;
            Q1=makeQuery(id+"F49.imprint","IMPRINT",FACE,{"disambiguationData":[TD([[makeQuery(id+"F49.imprint","IMPRINT",EDGE,{"derivedFrom":sQuery(id+"F49.wireOp",EDGE,"E49")}),1.0]])]});
            extrude(context, id + "F50", {"entities" : qUnion([Q0, Q1]), "operationType" : NewBodyOperationType.ADD, "oppositeDirection" : true, "depth" : 460 * mm});
        }
        {
            var Q0;
            Q0=makeQuery(id+"F48.opBoolean","MERGE",FACE,{"derivedFrom":[makeQuery(id+"F44.opExtrude","SWEPT_FACE",FACE,{"disambiguationData":[OSD([sQuery(id+"F43.wireOp",EDGE,"E43.right")])]}),makeQuery(id+"F46.opExtrude","CAP_FACE",FACE,{"disambiguationData":[OSD([sQuery(id+"F45.wireOp",EDGE,"E48.bottom"),sQuery(id+"F45.wireOp",EDGE,"E48.top"),sQuery(id+"F45.wireOp",EDGE,"E48.left"),sQuery(id+"F45.wireOp",EDGE,"E48.right")])],"isStart":false})]});
            var sketch = newSketch(context, id + "F51", { "sketchPlane" : qUnion([Q0])});
            skLineSegment(sketch, "E61", {"start": v(-294.22, 281.88) * mm, "end": v(-434.22, 281.88) * mm});
            skLineSegment(sketch, "E62", {"start": v(-434.22, 281.88) * mm, "end": v(-478.01, 206.03) * mm});
            skLineSegment(sketch, "E63", {"start": v(-478.01, 206.03) * mm, "end": v(-294.22, 200) * mm});
            skLineSegment(sketch, "E64", {"start": v(-294.22, 200) * mm, "end": v(-294.22, 281.88) * mm});
            skSolve(sketch);
        }
        {
            var Q0;
            Q0 = qSketchRegion(id + "F51", true);
            extrude(context, id + "F52", {"entities" : qUnion([Q0]), "operationType" : NewBodyOperationType.ADD, "depth" : 1 * mm});
        }
        {
            var Q0;
            Q0=makeQuery(id+"F48.opBoolean","MERGE",FACE,{"derivedFrom":[makeQuery(id+"F44.opExtrude","SWEPT_FACE",FACE,{"disambiguationData":[OSD([sQuery(id+"F43.wireOp",EDGE,"E43.left")])]}),makeQuery(id+"F46.opExtrude","CAP_FACE",FACE,{"disambiguationData":[OSD([sQuery(id+"F45.wireOp",EDGE,"E48.bottom"),sQuery(id+"F45.wireOp",EDGE,"E48.top"),sQuery(id+"F45.wireOp",EDGE,"E48.left"),sQuery(id+"F45.wireOp",EDGE,"E48.right")])],"isStart":true})]});
            var sketch = newSketch(context, id + "F53", { "sketchPlane" : qUnion([Q0])});
            skLineSegment(sketch, "E65", {"start": v(294.22, 281.88) * mm, "end": v(434.22, 281.88) * mm});
            skLineSegment(sketch, "E66", {"start": v(434.22, 281.88) * mm, "end": v(478.01, 206.03) * mm});
            skLineSegment(sketch, "E67", {"start": v(478.01, 206.03) * mm, "end": v(294.22, 199.98) * mm});
            skLineSegment(sketch, "E68", {"start": v(294.22, 199.98) * mm, "end": v(294.22, 281.88) * mm});
            skSolve(sketch);
        }
        {
            var Q0;
            Q0 = qSketchRegion(id + "F53", true);
            extrude(context, id + "F54", {"entities" : qUnion([Q0]), "operationType" : NewBodyOperationType.ADD, "depth" : 1 * mm});
        }
        {
            var Q0;
            Q0=makeQuery(id+"F8.opExtrude","CAP_FACE",FACE,{"disambiguationData":[OSD([sQuery(id+"F7.wireOp",EDGE,"E3")])],"isStart":false});
            var sketch = newSketch(context, id + "F55", { "sketchPlane" : qUnion([Q0])});
            skLineSegment(sketch, "E69.bottom", {"start": v(265, -81.79) * mm, "end": v(-265, -81.79) * mm});
            skLineSegment(sketch, "E69.top", {"start": v(265, 48.21) * mm, "end": v(-265, 48.21) * mm});
            skLineSegment(sketch, "E69.left", {"start": v(265, -81.79) * mm, "end": v(265, 48.21) * mm});
            skLineSegment(sketch, "E69.right", {"start": v(-265, -81.79) * mm, "end": v(-265, 48.21) * mm});
            skPoint(sketch, "E69.middle", {"position": v(0, -16.79) * mm});
            skCircle(sketch, "E70.0", {"center": v(-200, -16.79) * mm, "radius": 25 * mm});
            skCircle(sketch, "E71.0", {"center": v(0, -16.79) * mm, "radius": 25 * mm});
            skCircle(sketch, "E72.0", {"center": v(200, -16.79) * mm, "radius": 25 * mm});
            skSolve(sketch);
        }
        {
            var Q0;
            Q0 = qSketchRegion(id + "F55", true);
            extrude(context, id + "F56", {"entities" : qUnion([Q0]), "depth" : 1 * mm});
        }
        {
            var Q0;
            Q0=makeQuery(id+"F56.opExtrude","CAP_FACE",FACE,{"disambiguationData":[OSD([sQuery(id+"F55.wireOp",EDGE,"E69.bottom"),sQuery(id+"F55.wireOp",EDGE,"E69.top"),sQuery(id+"F55.wireOp",EDGE,"E69.left"),sQuery(id+"F55.wireOp",EDGE,"E69.right"),sQuery(id+"F55.wireOp",EDGE,"E72.0"),sQuery(id+"F55.wireOp",EDGE,"E71.0"),sQuery(id+"F55.wireOp",EDGE,"E70.0")])],"isStart":false});
            var sketch = newSketch(context, id + "F57", { "sketchPlane" : qUnion([Q0])});
            skLineSegment(sketch, "E73", {"start": v(-265, 48.21) * mm, "end": v(-265, -81.79) * mm});
            skLineSegment(sketch, "E74", {"start": v(-265, -81.79) * mm, "end": v(265, -81.79) * mm});
            skLineSegment(sketch, "E75", {"start": v(265, -81.79) * mm, "end": v(265, 48.21) * mm});
            skLineSegment(sketch, "E76", {"start": v(265, 48.21) * mm, "end": v(264, 48.21) * mm});
            skLineSegment(sketch, "E77", {"start": v(264, 48.21) * mm, "end": v(264, -80.79) * mm});
            skLineSegment(sketch, "E78", {"start": v(264, -80.79) * mm, "end": v(-264, -80.79) * mm});
            skLineSegment(sketch, "E79", {"start": v(-264, -80.79) * mm, "end": v(-264, 48.21) * mm});
            skLineSegment(sketch, "E80", {"start": v(-264, 48.21) * mm, "end": v(-265, 48.21) * mm});
            skSolve(sketch);
        }
        {
            var Q0;
            Q0 = qSketchRegion(id + "F57", true);
            extrude(context, id + "F58", {"entities" : qUnion([Q0]), "operationType" : NewBodyOperationType.ADD, "depth" : 100 * mm});
        }
        {
            var Q0;
            Q0=makeQuery(id+"F58.boolean.opBoolean","MERGE",FACE,{"derivedFrom":[makeQuery(id+"F56.opExtrude","SWEPT_FACE",FACE,{"disambiguationData":[OSD([sQuery(id+"F55.wireOp",EDGE,"E69.left")])]}),makeQuery(id+"F58.opExtrude","SWEPT_FACE",FACE,{"disambiguationData":[OSD([sQuery(id+"F57.wireOp",EDGE,"E75")])]})]});
            var sketch = newSketch(context, id + "F59", { "sketchPlane" : qUnion([Q0])});
            skLineSegment(sketch, "E81", {"start": v(-662.69, 288.17) * mm, "end": v(-663.55, 288.66) * mm});
            skLineSegment(sketch, "E82", {"start": v(-663.55, 288.66) * mm, "end": v(-598.58, 401.2) * mm});
            skLineSegment(sketch, "E83", {"start": v(-598.58, 401.2) * mm, "end": v(-597.69, 400.75) * mm});
            skLineSegment(sketch, "E84", {"start": v(-597.69, 400.75) * mm, "end": v(-662.69, 288.17) * mm});
            skSolve(sketch);
        }
        {
            var Q0;
            Q0 = qSketchRegion(id + "F59", true);
            extrude(context, id + "F60", {"entities" : qUnion([Q0]), "oppositeDirection" : true, "depth" : 530 * mm});
        }
        {
            var Q0;
            Q0=makeQuery(id+"F54.boolean.opBoolean","MERGE",FACE,{"derivedFrom":[makeQuery(id+"F50.opExtrude","SWEPT_FACE",FACE,{"disambiguationData":[OSD([sQuery(id+"F49.wireOp",EDGE,"E53")])]}),makeQuery(id+"F54.opExtrude","CAP_FACE",FACE,{"disambiguationData":[OSD([sQuery(id+"F53.wireOp",EDGE,"E65"),sQuery(id+"F53.wireOp",EDGE,"E66"),sQuery(id+"F53.wireOp",EDGE,"E67"),sQuery(id+"F53.wireOp",EDGE,"E68")])],"isStart":false})]});
            var Q1;
            Q1=makeQuery(id+"F52.boolean.opBoolean","MERGE",FACE,{"derivedFrom":[makeQuery(id+"F50.opExtrude","SWEPT_FACE",FACE,{"disambiguationData":[OSD([sQuery(id+"F49.wireOp",EDGE,"E59")])]}),makeQuery(id+"F52.opExtrude","CAP_FACE",FACE,{"disambiguationData":[OSD([sQuery(id+"F51.wireOp",EDGE,"E61"),sQuery(id+"F51.wireOp",EDGE,"E62"),sQuery(id+"F51.wireOp",EDGE,"E63"),sQuery(id+"F51.wireOp",EDGE,"E64")])],"isStart":false})]});
            cPlane(context, id + "F61", {"entities" : qUnion([Q0, Q1]), "cplaneType" : CPlaneType.MID_PLANE, "offset" : 25 * mm, "width" : 150 * mm, "height" : 150 * mm});
        }
        {
            var Q0;
            Q0=qCreatedBy(id+"F61.planeOp",FACE);
            var sketch = newSketch(context, id + "F62", { "sketchPlane" : qUnion([Q0])});
            skCircle(sketch, "E85", {"center": v(208.25, 384.45) * mm, "radius": 95.8 * mm});
            skSolve(sketch);
        }
        {
            var Q0;
            Q0 = qSketchRegion(id + "F62", true);
            extrude(context, id + "F63", {"entities" : qUnion([Q0]), "endBound" : BoundingType.SYMMETRIC, "depth" : 100 * mm});
        }
        {
            var Q0;
            Q0=makeQuery(id+"F54.boolean.opBoolean","MERGE",FACE,{"derivedFrom":[makeQuery(id+"F52.boolean.opBoolean","MERGE",FACE,{"derivedFrom":[makeQuery(id+"F44.opExtrude","CAP_FACE",FACE,{"disambiguationData":[OSD([sQuery(id+"F43.wireOp",EDGE,"E43.bottom"),sQuery(id+"F43.wireOp",EDGE,"E43.top"),sQuery(id+"F43.wireOp",EDGE,"E43.left"),sQuery(id+"F43.wireOp",EDGE,"E43.right"),sQuery(id+"F43.wireOp",EDGE,"E44.0"),sQuery(id+"F43.wireOp",EDGE,"E45.0"),sQuery(id+"F43.wireOp",EDGE,"E46.0")])],"isStart":true}),makeQuery(id+"F52.opExtrude","SWEPT_FACE",FACE,{"disambiguationData":[OSD([sQuery(id+"F51.wireOp",EDGE,"E62")])]})]}),makeQuery(id+"F54.opExtrude","SWEPT_FACE",FACE,{"disambiguationData":[OSD([sQuery(id+"F53.wireOp",EDGE,"E66")])]})]});
            cPlane(context, id + "F64", {"entities" : qUnion([Q0]), "cplaneType" : CPlaneType.OFFSET, "offset" : 40 * mm, "oppositeDirection" : true, "width" : 150 * mm, "height" : 150 * mm});
        }
        {
            var Q0;
            Q0=qCreatedBy(id+"F64.planeOp",FACE);
            var sketch = newSketch(context, id + "F65", { "sketchPlane" : qUnion([Q0])});
            skCircle(sketch, "E86", {"center": v(0, 272.95) * mm, "radius": 45 * mm});
            skSolve(sketch);
        }
        {
            var Q0;
            Q0 = qSketchRegion(id + "F65", true);
            extrude(context, id + "F66", {"entities" : qUnion([Q0]), "operationType" : NewBodyOperationType.ADD, "oppositeDirection" : true, "depth" : 100 * mm});
        }
        {
            var Q0;
            Q0=makeQuery(id+"F60.opExtrude","SWEPT_FACE",FACE,{"disambiguationData":[OSD([sQuery(id+"F59.wireOp",EDGE,"E82")])]});
            extrude(context, id + "F67", {"entities" : qUnion([Q0]), "oppositeDirection" : true, "depth" : 110 * mm});
        }
        {
            var Q0;
            Q0=makeQuery(id+"F66.opExtrude","CAP_FACE",FACE,{"disambiguationData":[OSD([sQuery(id+"F65.wireOp",EDGE,"E86")])],"isStart":true});
            var Q1;
            Q1=makeQuery(id+"F67.opExtrude","SWEPT_FACE",FACE,{"disambiguationData":[OSD([sQuery(id+"F59.wireOp",EDGE,"E82"),sQuery(id+"F59.wireOp",EDGE,"E83")])]});
            loft(context, id + "F68", {"startCondition" : LoftEndDerivativeType.NORMAL_TO_PROFILE, "startMagnitude" : 3, "endCondition" : LoftEndDerivativeType.NORMAL_TO_PROFILE, "endMagnitude" : 1, "sheetProfilesArray" : [{ "sheetProfileEntities" : qUnion([Q0]) }, { "sheetProfileEntities" : qUnion([Q1]) }]});
        }
        {
            var Q0;
            Q0=makeQuery(id+"F63.opExtrude","CAP_FACE",FACE,{"disambiguationData":[OSD([sQuery(id+"F62.wireOp",EDGE,"E85")])],"isStart":false});
            var sketch = newSketch(context, id + "F69", { "sketchPlane" : qUnion([Q0])});
            skCircle(sketch, "E87", {"center": v(208.25, 384.45) * mm, "radius": 60 * mm});
            skSolve(sketch);
        }
        {
            var Q0;
            Q0 = qSketchRegion(id + "F69", true);
            extrude(context, id + "F70", {"entities" : qUnion([Q0]), "operationType" : NewBodyOperationType.ADD, "depth" : 150 * mm});
        }
        {
            var Q0;
            Q0=qCreatedBy(id+"F61.planeOp",FACE);
            var sketch = newSketch(context, id + "F71", { "sketchPlane" : qUnion([Q0])});
            skLineSegment(sketch, "E88.bottom", {"start": v(-139.4, 431.88) * mm, "end": v(60.6, 431.88) * mm});
            skLineSegment(sketch, "E88.top", {"start": v(-139.4, 281.88) * mm, "end": v(60.6, 281.88) * mm});
            skLineSegment(sketch, "E88.left", {"start": v(-139.4, 431.88) * mm, "end": v(-139.4, 281.88) * mm});
            skLineSegment(sketch, "E88.right", {"start": v(60.6, 431.88) * mm, "end": v(60.6, 281.88) * mm});
            skSolve(sketch);
        }
        {
            var Q0;
            Q0 = qSketchRegion(id + "F71", true);
            extrude(context, id + "F72", {"entities" : qUnion([Q0]), "endBound" : BoundingType.SYMMETRIC, "depth" : 200 * mm});
        }
    });
